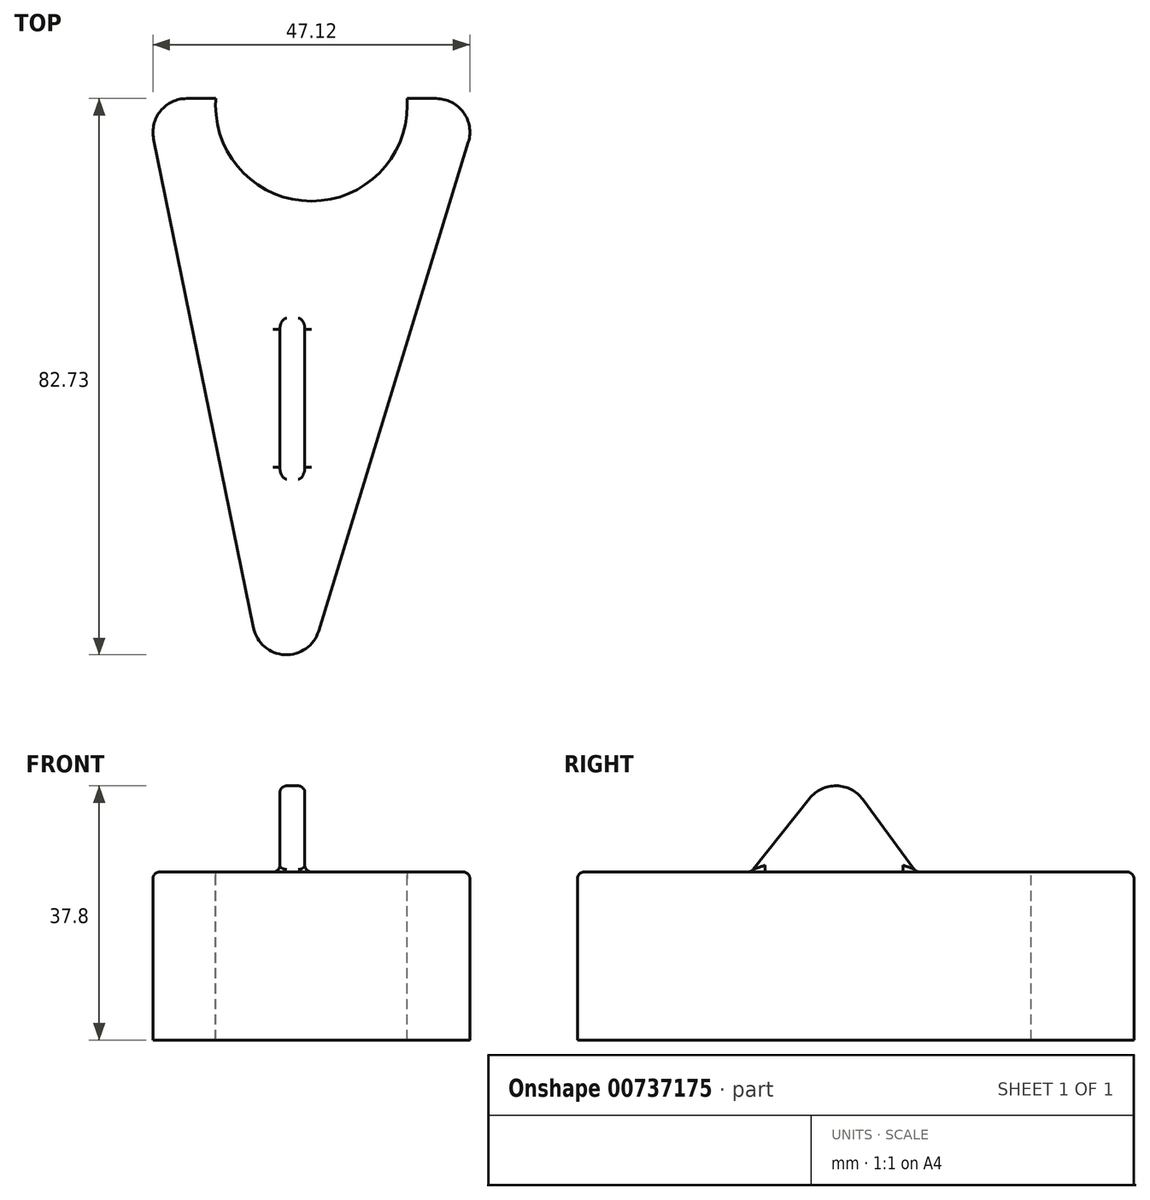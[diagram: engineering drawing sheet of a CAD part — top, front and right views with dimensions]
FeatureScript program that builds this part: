
annotation { "Feature Type Name" : "Feature", "Feature Type Description" : "" }
export const myFeature = defineFeature(function(context is Context, id is Id, definition is map)
    precondition{}
    {
        {
            var Q0;
            Q0=qCreatedBy(makeId("Top.planeOp"),FACE);
            var sketch = newSketch(context, id + "F0", { "sketchPlane" : qUnion([Q0])});
            skLineSegment(sketch, "E0", {"start": v(-18.78, 14) * mm, "end": v(-3.93, -58.73) * mm});
            skLineSegment(sketch, "E1", {"start": v(5.75, -59.2) * mm, "end": v(28.02, 13.54) * mm});
            skLineSegment(sketch, "E2", {"start": v(23.24, 20) * mm, "end": v(-13.88, 20) * mm});
            skPoint(sketch, "E3.visualSharp", {"position": v(0, -77.98) * mm});
            skArc(sketch, "E3.filletArc", {"start": v(-3.93, -58.73) * mm, "mid": v(0.73, -62.73) * mm, "end": v(5.75, -59.2) * mm});
            skPoint(sketch, "E4.visualSharp", {"position": v(30, 20) * mm});
            skArc(sketch, "E4.filletArc", {"start": v(28.02, 13.54) * mm, "mid": v(27.26, 17.97) * mm, "end": v(23.24, 20) * mm});
            skPoint(sketch, "E5.visualSharp", {"position": v(-20, 20) * mm});
            skArc(sketch, "E5.filletArc", {"start": v(-13.88, 20) * mm, "mid": v(-17.75, 18.16) * mm, "end": v(-18.78, 14) * mm});
            skSolve(sketch);
        }
        {
            var Q0;
            Q0 = qSketchRegion(id + "F0", true);
            extrude(context, id + "F1", {"entities" : qUnion([Q0]), "depth" : 25 * mm, "offsetDistance" : 25 * mm});
        }
        {
            var Q0;
            Q0=qCreatedBy(makeId("Right.planeOp"),FACE);
            cPlane(context, id + "F2", {"entities" : qUnion([Q0]), "cplaneType" : CPlaneType.OFFSET, "offset" : 0 * mm, "oppositeDirection" : true, "width" : 150 * mm, "height" : 150 * mm});
        }
        {
            var Q0;
            Q0=qCreatedBy(id+"F2.planeOp",FACE);
            var sketch = newSketch(context, id + "F3", { "sketchPlane" : qUnion([Q0])});
            skLineSegment(sketch, "E6.0", {"start": v(-12.36, 25) * mm, "end": v(-36.9, 25) * mm});
            skLineSegment(sketch, "E7", {"start": v(-12.36, 25) * mm, "end": v(-20.29, 35.77) * mm});
            skLineSegment(sketch, "E8", {"start": v(-28.23, 35.91) * mm, "end": v(-36.9, 25) * mm});
            skPoint(sketch, "E9.orphan", {"position": v(14, 25) * mm});
            skPoint(sketch, "E10.visualSharp", {"position": v(-24.16, 41.03) * mm});
            skArc(sketch, "E10.filletArc", {"start": v(-20.29, 35.77) * mm, "mid": v(-24.22, 37.8) * mm, "end": v(-28.23, 35.91) * mm});
            skSolve(sketch);
        }
        {
            var Q0;
            Q0=makeQuery(id+"F3.imprint","IMPRINT",FACE,{"disambiguationData":[TD([[makeQuery(id+"F3.imprint","IMPRINT",EDGE,{"derivedFrom":sQuery(id+"F3.wireOp",EDGE,"E6.0")}),-1.0]])]});
            extrude(context, id + "F4", {"entities" : qUnion([Q0]), "operationType" : NewBodyOperationType.ADD, "depth" : 3.7 * mm, "offsetDistance" : 25 * mm});
        }
        {
            var Q0;
            Q0=makeQuery(id+"F1.opExtrude","CAP_FACE",FACE,{"disambiguationData":[OSD([sQuery(id+"F0.wireOp",EDGE,"E0"),sQuery(id+"F0.wireOp",EDGE,"E1"),sQuery(id+"F0.wireOp",EDGE,"E2")])],"isStart":false});
            var Q1;
            Q1=makeQuery(id+"F4.opExtrude","SWEPT_FACE",FACE,{"disambiguationData":[OSD([sQuery(id+"F3.wireOp",EDGE,"E8")])]});
            fillet(context, id + "F5", {"entities" : qUnion([Q0, Q1]), "radius" : 1 * mm, "tangentPropagation" : true, "allowEdgeOverflow" : false});
        }
        {
            var Q0;
            Q0=makeQuery(id+"F1.opExtrude","CAP_FACE",FACE,{"disambiguationData":[OSD([sQuery(id+"F0.wireOp",EDGE,"E0"),sQuery(id+"F0.wireOp",EDGE,"E1"),sQuery(id+"F0.wireOp",EDGE,"E2"),sQuery(id+"F0.wireOp",EDGE,"E3.filletArc"),sQuery(id+"F0.wireOp",EDGE,"E4.filletArc"),sQuery(id+"F0.wireOp",EDGE,"E5.filletArc")])],"isStart":false});
            var sketch = newSketch(context, id + "F6", { "sketchPlane" : qUnion([Q0])});
            skCircle(sketch, "E11", {"center": v(4.68, 19) * mm, "radius": 14.25 * mm});
            skSolve(sketch);
        }
        {
            var Q0;
            Q0 = qSketchRegion(id + "F6", true);
            extrude(context, id + "F7", {"entities" : qUnion([Q0]), "operationType" : NewBodyOperationType.REMOVE, "oppositeDirection" : true, "depth" : 25 * mm, "offsetDistance" : 25 * mm});
        }
    });
